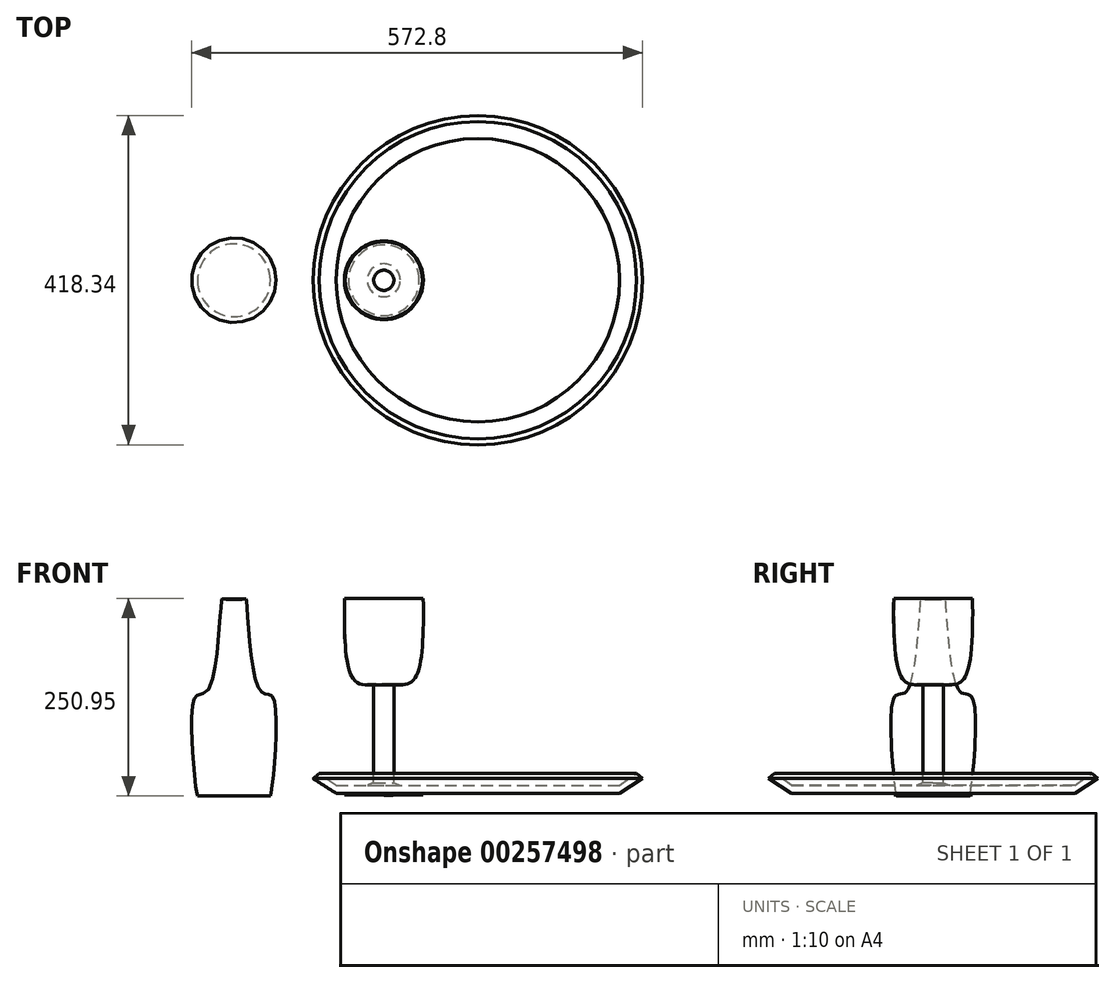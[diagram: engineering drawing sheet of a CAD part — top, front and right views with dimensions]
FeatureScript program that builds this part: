
annotation { "Feature Type Name" : "Feature", "Feature Type Description" : "" }
export const myFeature = defineFeature(function(context is Context, id is Id, definition is map)
    precondition{}
    {
        {
            var Q0;
            Q0=qCreatedBy(makeId("Front.planeOp"),FACE);
            var sketch = newSketch(context, id + "F0", { "sketchPlane" : qUnion([Q0])});
            skLineSegment(sketch, "E0", {"start": v(0, 109.46) * mm, "end": v(0, -140.54) * mm});
            skLineSegment(sketch, "E1", {"start": v(0, 109.46) * mm, "end": v(50, 109.46) * mm});
            skFitSpline(sketch, "E2", {"points": [v(50, 109.46) * mm, v(38.12, 6.24) * mm, v(12.8, 0) * mm], "startDerivative": vector(3.26, -204.88) * mm, "endDerivative": vector(-96.43, 7.01) * mm});
            skLineSegment(sketch, "E3", {"start": v(12.8, 0) * mm, "end": v(12.8, -124.66) * mm});
            skLineSegment(sketch, "E4", {"start": v(12.8, -124.66) * mm, "end": v(50, -140.28) * mm});
            skLineSegment(sketch, "E5", {"start": v(50, -140.28) * mm, "end": v(0, -140.54) * mm});
            skLineSegment(sketch, "E6", {"start": v(12.8, 0) * mm, "end": v(0, 0) * mm});
            skSolve(sketch);
        }
        {
            var Q0;
            Q0=makeQuery(id+"F0.imprint","IMPRINT",FACE,{"disambiguationData":[TD([[makeQuery(id+"F0.imprint","IMPRINT",EDGE,{"derivedFrom":sQuery(id+"F0.wireOp",EDGE,"E0")}),1.0]])]});
            var Q1;
            Q1=sQuery(id+"F0.wireOp",EDGE,"E0");
            revolve(context, id + "F1", {"entities" : qUnion([Q0]), "axis" : qUnion([Q1]), "revolveType" : RevolveType.FULL});
        }
        {
            var Q0;
            Q0=makeQuery(id+"F1.opRevolve","SWEPT_FACE",FACE,{"disambiguationData":[OSD([sQuery(id+"F0.wireOp",EDGE,"E1")])]});
            shell(context, id + "F2", {"entities" : qUnion([Q0]), "thickness" : 1 * mm});
        }
        {
            var Q0;
            Q0=makeQuery(id+"F0.imprint","IMPRINT",FACE,{"disambiguationData":[TD([[makeQuery(id+"F0.imprint","IMPRINT",EDGE,{"derivedFrom":sQuery(id+"F0.wireOp",EDGE,"E3")}),-1.0]])]});
            var Q1;
            Q1=sQuery(id+"F0.wireOp",EDGE,"E0");
            revolve(context, id + "F3", {"operationType" : NewBodyOperationType.ADD, "entities" : qUnion([Q0]), "axis" : qUnion([Q1]), "revolveType" : RevolveType.FULL});
        }
        {
            var Q0;
            Q0=qCreatedBy(makeId("Front.planeOp"),FACE);
            var sketch = newSketch(context, id + "F4", { "sketchPlane" : qUnion([Q0])});
            skLineSegment(sketch, "E7", {"start": v(-190.4, -141.5) * mm, "end": v(-190.4, 108.5) * mm});
            skFitSpline(sketch, "E8", {"points": [v(-190.4, 108.5) * mm, v(-175.73, 108.5) * mm, v(-175.08, 108.5) * mm, v(-157.14, -7.86) * mm, v(-140.84, -16.34) * mm, v(-144.13, -141.5) * mm, v(-144.42, -141.5) * mm], "startDerivative": vector(160.21, -8.1) * mm, "endDerivative": vector(-16.76, 14.37) * mm});
            skLineSegment(sketch, "E9", {"start": v(-190.4, -141.5) * mm, "end": v(-144.13, -141.5) * mm});
            skSolve(sketch);
        }
        {
            var Q0;
            {var subQ0=sQuery(id+"F4.wireOp",EDGE,"E7");Q0=makeQuery(id+"F4.imprint","IMPRINT",FACE,{"disambiguationData":[TD([[makeQuery(id+"F4.imprint","IMPRINT",EDGE,{"derivedFrom":subQ0}),-1.0]])]});}
            var Q1;
            Q1=sQuery(id+"F4.wireOp",EDGE,"E7");
            revolve(context, id + "F5", {"entities" : qUnion([Q0]), "axis" : qUnion([Q1]), "revolveType" : RevolveType.FULL});
        }
        {
            var Q0;
            Q0=qCreatedBy(makeId("Front.planeOp"),FACE);
            var sketch = newSketch(context, id + "F6", { "sketchPlane" : qUnion([Q0])});
            skLineSegment(sketch, "E10", {"start": v(119.44, -138.1) * mm, "end": v(119.44, -128.1) * mm});
            skLineSegment(sketch, "E11", {"start": v(119.44, -128.1) * mm, "end": v(299.44, -128.1) * mm});
            skLineSegment(sketch, "E12", {"start": v(299.44, -128.1) * mm, "end": v(320.97, -112.97) * mm});
            skLineSegment(sketch, "E13", {"start": v(320.97, -112.97) * mm, "end": v(328.6, -119.42) * mm});
            skLineSegment(sketch, "E14", {"start": v(119.44, -138.1) * mm, "end": v(299.44, -138.1) * mm});
            skLineSegment(sketch, "E15", {"start": v(299.44, -138.1) * mm, "end": v(328.6, -119.42) * mm});
            skSolve(sketch);
        }
        {
            var Q0;
            Q0=makeQuery(id+"F6.imprint","IMPRINT",FACE,{"disambiguationData":[TD([[makeQuery(id+"F6.imprint","IMPRINT",EDGE,{"derivedFrom":sQuery(id+"F6.wireOp",EDGE,"E10")}),-1.0]])]});
            var Q1;
            Q1=sQuery(id+"F6.wireOp",EDGE,"E10");
            revolve(context, id + "F7", {"operationType" : NewBodyOperationType.ADD, "entities" : qUnion([Q0]), "axis" : qUnion([Q1]), "revolveType" : RevolveType.FULL});
        }
    });
